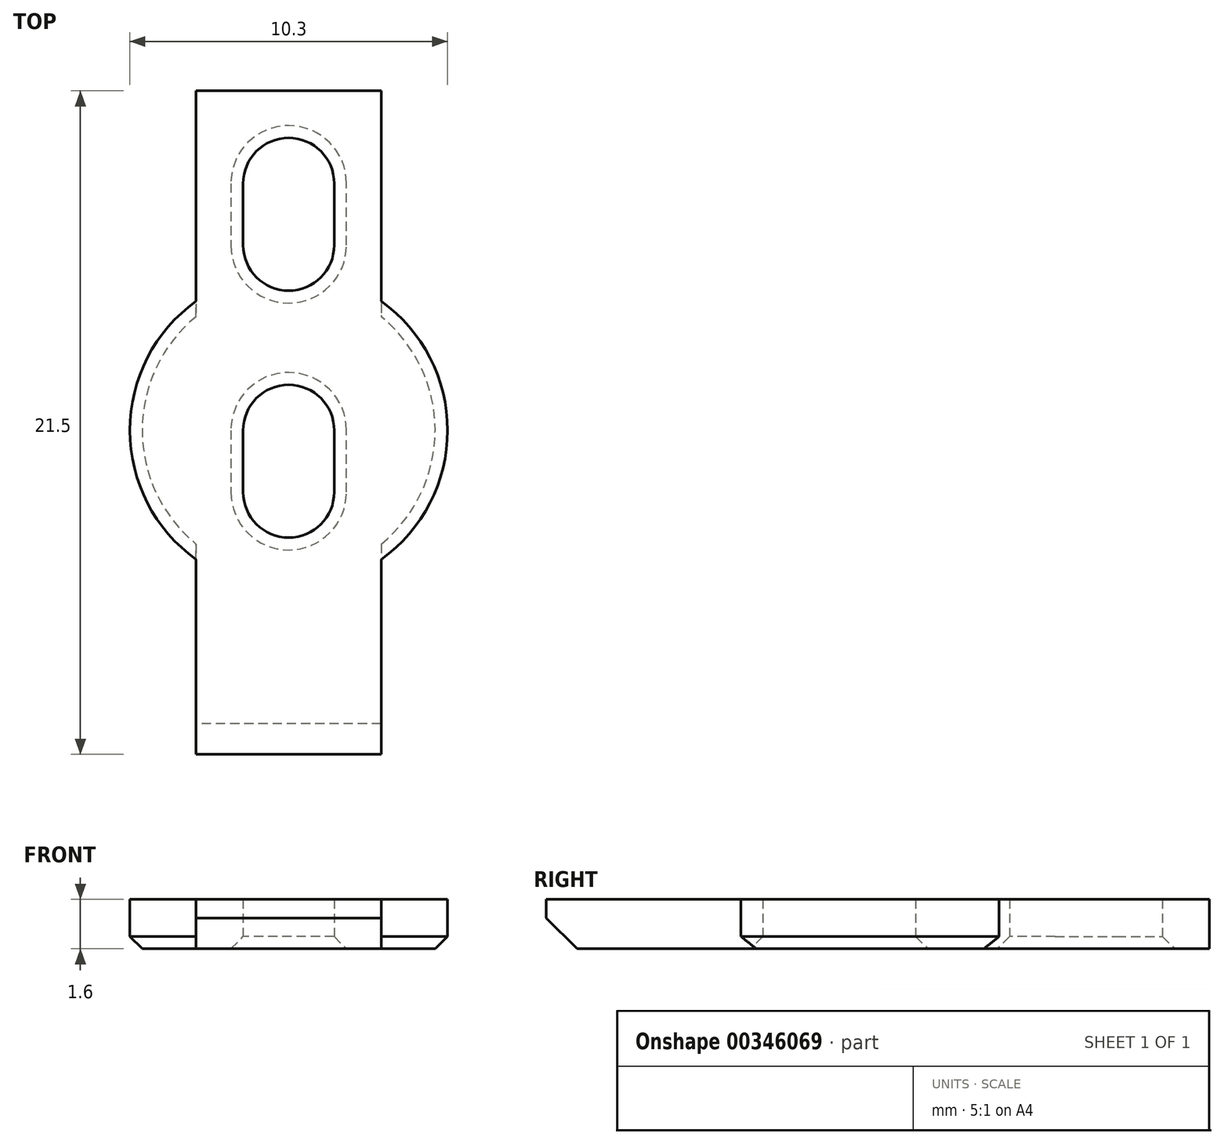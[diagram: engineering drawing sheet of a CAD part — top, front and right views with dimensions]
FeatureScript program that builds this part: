
annotation { "Feature Type Name" : "Feature", "Feature Type Description" : "" }
export const myFeature = defineFeature(function(context is Context, id is Id, definition is map)
    precondition{}
    {
        {
            var Q0;
            Q0=qCreatedBy(makeId("Top.planeOp"),FACE);
            var sketch = newSketch(context, id + "F0", { "sketchPlane" : qUnion([Q0])});
            skCircle(sketch, "E0", {"center": v(0, 0) * mm, "radius": 5.15 * mm});
            skLineSegment(sketch, "E1.bottom", {"start": v(-3, 11) * mm, "end": v(3, 11) * mm});
            skLineSegment(sketch, "E1.top", {"start": v(-3, -10.5) * mm, "end": v(3, -10.5) * mm});
            skLineSegment(sketch, "E1.left", {"start": v(-3, 11) * mm, "end": v(-3, -10.5) * mm});
            skLineSegment(sketch, "E1.right", {"start": v(3, 11) * mm, "end": v(3, -10.5) * mm});
            skLineSegment(sketch, "E2", {"start": v(0, 11) * mm, "end": v(0, 7) * mm, "construction": true});
            skLineSegment(sketch, "E3", {"start": v(0, 7) * mm, "end": v(0, -1) * mm, "construction": true});
            skLineSegment(sketch, "E4", {"start": v(0, -1) * mm, "end": v(0, -10.5) * mm, "construction": true});
            skArc(sketch, "E5", {"start": v(1.48, 0) * mm, "mid": v(0, 1.48) * mm, "end": v(-1.48, 0) * mm});
            skArc(sketch, "E6", {"start": v(-1.48, -2) * mm, "mid": v(0, -3.48) * mm, "end": v(1.48, -2) * mm});
            skLineSegment(sketch, "E7", {"start": v(-1.47, 0) * mm, "end": v(-1.47, -2) * mm});
            skLineSegment(sketch, "E8", {"start": v(1.48, 0) * mm, "end": v(1.48, -2) * mm});
            skLineSegment(sketch, "E9", {"start": v(1.48, -1) * mm, "end": v(0, -1) * mm, "construction": true});
            skArc(sketch, "E10", {"start": v(1.48, 8) * mm, "mid": v(0, 9.48) * mm, "end": v(-1.48, 8) * mm});
            skArc(sketch, "E11", {"start": v(-1.48, 6) * mm, "mid": v(0, 4.52) * mm, "end": v(1.48, 6) * mm});
            skLineSegment(sketch, "E12", {"start": v(1.48, 8) * mm, "end": v(1.48, 6) * mm});
            skLineSegment(sketch, "E13", {"start": v(-1.48, 8) * mm, "end": v(-1.48, 6) * mm});
            skLineSegment(sketch, "E14", {"start": v(0, 7) * mm, "end": v(1.48, 7) * mm, "construction": true});
            skSolve(sketch);
        }
        {
            var Q0;
            Q0 = qSketchRegion(id + "F0", true);
            extrude(context, id + "F1", {"entities" : qUnion([Q0]), "depth" : 1.6 * mm});
        }
        {
            var Q0;
            {var subQ0=sQuery(id+"F0.wireOp",EDGE,"E1.left");var subQ1=sQuery(id+"F0.wireOp",EDGE,"E0");Q0=makeQuery(id+"F1.opExtrude","CAP_EDGE",EDGE,{"disambiguationData":[OSD([subQ1]),TDD([makeQuery(id+"F0.imprint","IMPRINT",EDGE,{"disambiguationData":[TD([[makeQuery(id+"F0.imprint","INTERSECT",VERTEX,{"disambiguationData":[OD(0.0)],"derivedFrom":[subQ1,subQ0]}),-1.0]])],"derivedFrom":subQ1})])],"isStart":true});}
            var Q1;
            {var subQ0=sQuery(id+"F0.wireOp",EDGE,"E1.right");var subQ1=sQuery(id+"F0.wireOp",EDGE,"E0");Q1=makeQuery(id+"F1.opExtrude","CAP_EDGE",EDGE,{"disambiguationData":[OSD([subQ1]),TDD([makeQuery(id+"F0.imprint","IMPRINT",EDGE,{"disambiguationData":[TD([[makeQuery(id+"F0.imprint","INTERSECT",VERTEX,{"disambiguationData":[OD(0.0)],"derivedFrom":[subQ1,subQ0]}),1.0]])],"derivedFrom":subQ1})])],"isStart":true});}
            var Q2;
            Q2=makeQuery(id+"F1.opExtrude","CAP_EDGE",EDGE,{"disambiguationData":[OSD([sQuery(id+"F0.wireOp",EDGE,"E8")])],"isStart":true});
            var Q3;
            Q3=makeQuery(id+"F1.opExtrude","CAP_EDGE",EDGE,{"disambiguationData":[OSD([sQuery(id+"F0.wireOp",EDGE,"E12")])],"isStart":true});
            chamfer(context, id + "F2", {"entities" : qUnion([Q0, Q1, Q2, Q3]), "width" : 0.4 * mm, "tangentPropagation" : true});
        }
        {
            var Q0;
            Q0=makeQuery(id+"F1.opExtrude","CAP_EDGE",EDGE,{"disambiguationData":[OSD([sQuery(id+"F0.wireOp",EDGE,"E1.top")])],"isStart":true});
            chamfer(context, id + "F3", {"entities" : qUnion([Q0]), "width" : 1 * mm, "tangentPropagation" : true});
        }
    });
